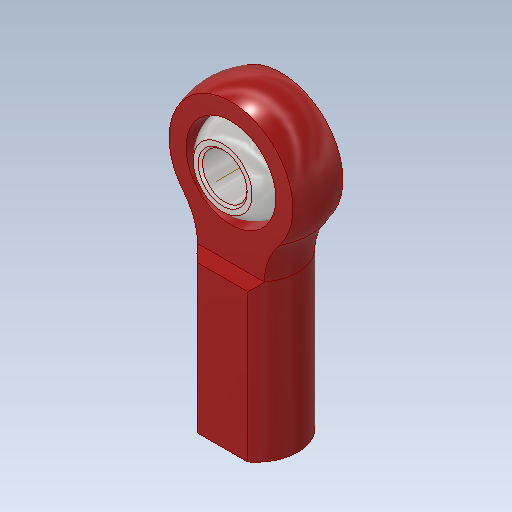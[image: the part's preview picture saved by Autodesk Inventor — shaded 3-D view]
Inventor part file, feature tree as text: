
AUTODESK INVENTOR PART (.ipt)
format: ipt  version: 2020 (Build 240168000, 168)  size: 603,136 bytes
history: native  units: in
note: dims shown in document units (in); Inventor stores cm internally (conversion verified against a paired STEP export)
features: other x4, plane x1
ambient origin geometry x8: Origin, YZ Plane, XZ Plane, XY Plane, X Axis, Y Axis, Z Axis, Center Point
bodies: Solid1 (feature_tree), Solid2 (feature_tree)
feature tree (5):
  plane  "Work Plane1"
  other  "Work Axis1"
  other  "Work Point1"
  parser-record x1  (decoder bookkeeping rows leaked as tree rows — omitted from the tree; the rows remain in map.json)
  other  "NONE:1"
